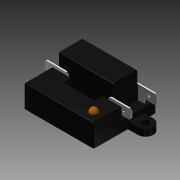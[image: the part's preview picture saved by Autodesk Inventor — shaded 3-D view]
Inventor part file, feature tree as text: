
AUTODESK INVENTOR PART (.ipt)
format: ipt  version: 2014 (Build 180170000, 170)  size: 413,184 bytes
history: native  units: mm (DEFAULTED — no unit token found)
features: sketch x3, fillet x2, plane x2, extrude x2, other x1, hole x1, mirror x1, imported_body x1
ambient origin geometry x8: Origin, YZ Plane, XZ Plane, XY Plane, X Axis, Y Axis, Z Axis, Center Point
bodies: Solid1 (feature_tree)
feature tree (13):
  other  "Spike Relay.ipt"
  fillet  "Fillet1"  Radius=0.762mm
  sketch  "Sketch2"  dims[d14=13.208mm d15=29.083mm]
  plane  "Work Plane1"
  extrude  "Extrusion1"  Depth=29.083mm
  extrude  "Extrusion2"  Depth=25.4mm TaperAngle=0.0deg
  hole  "Hole1"  [1 undecoded]
  plane  "Work Plane2"
  mirror  "Mirror2"
  fillet  "Fillet2"  [1 undecoded]
  imported_body  "DerivedBody::Spike Relay.ipt"
  sketch  "Sketch3"  dims[d16=34.0868mm d17=-4.318mm d18=25.4mm d19=0.0mm]
  sketch  "Sketch4"  dims[d20=25.4mm d21=0.0mm d22=4.4958mm d23=19.05mm d24=8.4328mm d25=6.35mm d26=14.3117mm d27=25.4mm d28=20.594885mm d29=0.635mm]
note: 2 required parameter values undecoded (feature->parameter linkage not recoverable at this tier; creation-order binding heuristic only, values carry confidence <= 0.55)
